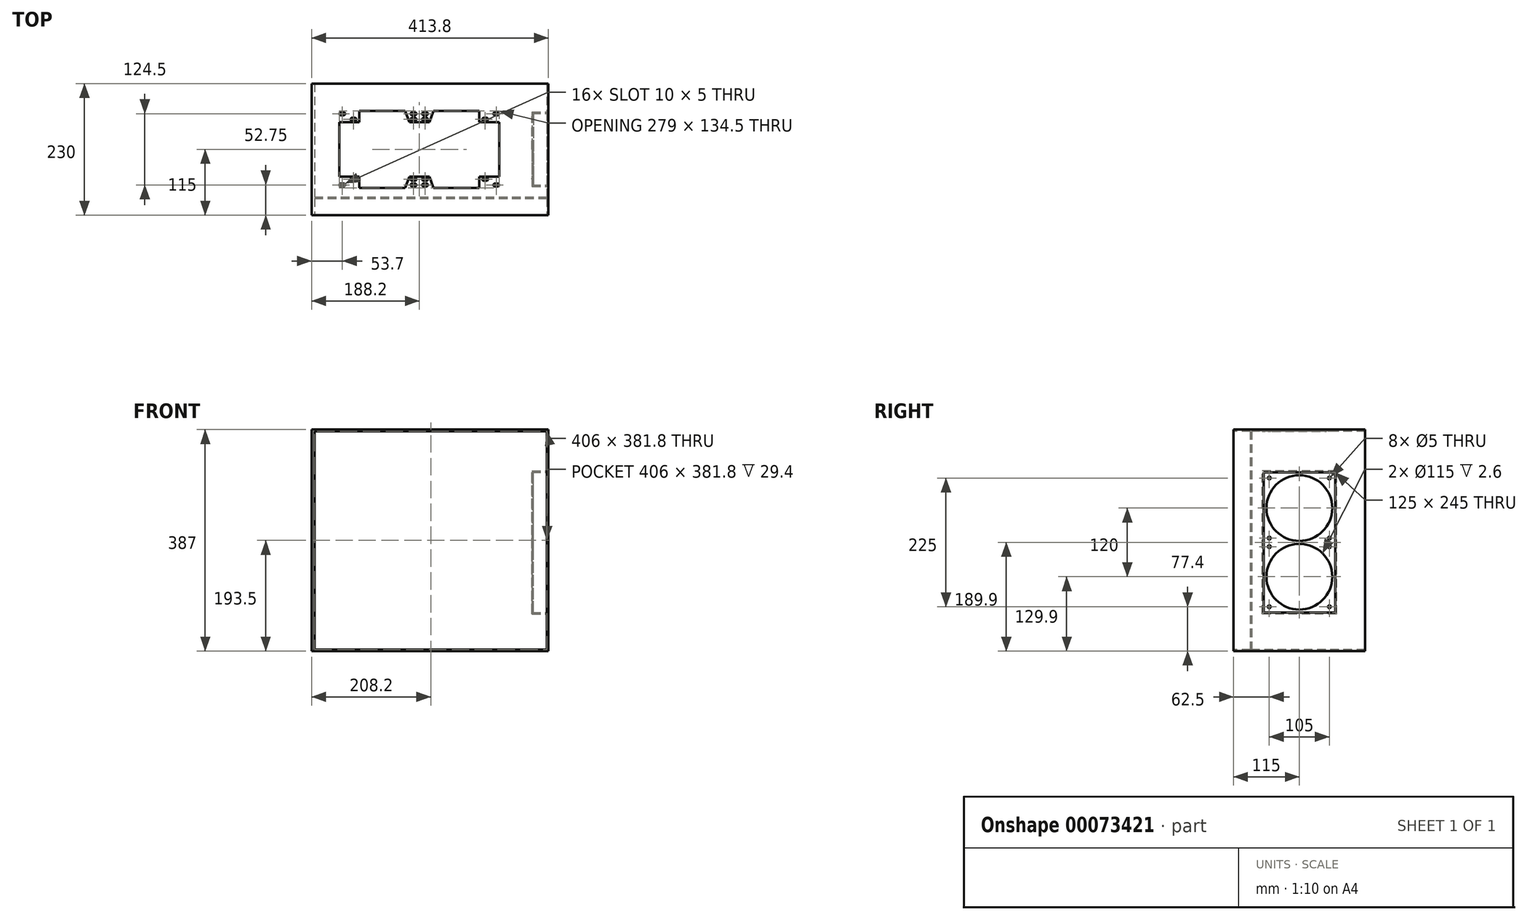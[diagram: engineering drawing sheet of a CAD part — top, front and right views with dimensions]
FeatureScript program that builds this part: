
annotation { "Feature Type Name" : "Feature", "Feature Type Description" : "" }
export const myFeature = defineFeature(function(context is Context, id is Id, definition is map)
    precondition{}
    {
        {
            var Q0;
            Q0=qCreatedBy(makeId("Front.planeOp"),FACE);
            var sketch = newSketch(context, id + "F0", { "sketchPlane" : qUnion([Q0])});
            skLineSegment(sketch, "E0.bottom", {"start": v(0, 0) * mm, "end": v(424, 0) * mm});
            skLineSegment(sketch, "E0.top", {"start": v(0, 397) * mm, "end": v(424, 397) * mm});
            skLineSegment(sketch, "E0.left", {"start": v(0, 0) * mm, "end": v(0, 397) * mm});
            skLineSegment(sketch, "E0.right", {"start": v(424, 0) * mm, "end": v(424, 397) * mm});
            skSolve(sketch);
        }
        {
            var Q0;
            Q0=makeQuery(id+"F0.imprint","IMPRINT",FACE,{"disambiguationData":[TD([[makeQuery(id+"F0.imprint","IMPRINT",EDGE,{"derivedFrom":sQuery(id+"F0.wireOp",EDGE,"E0.bottom")}),1.0]])]});
            extrude(context, id + "F1", {"entities" : qUnion([Q0]), "depth" : 230 * mm});
        }
        {
            var Q0;
            Q0=makeQuery(id+"F1.opExtrude","CAP_FACE",FACE,{"disambiguationData":[OSD([sQuery(id+"F0.wireOp",EDGE,"E0.bottom"),sQuery(id+"F0.wireOp",EDGE,"E0.top"),sQuery(id+"F0.wireOp",EDGE,"E0.left"),sQuery(id+"F0.wireOp",EDGE,"E0.right")])],"isStart":false});
            var sketch = newSketch(context, id + "F2", { "sketchPlane" : qUnion([Q0])});
            skLineSegment(sketch, "E1.bottom", {"start": v(5.2, 2.6) * mm, "end": v(411.2, 2.6) * mm});
            skLineSegment(sketch, "E1.top", {"start": v(5.2, 384.4) * mm, "end": v(411.2, 384.4) * mm});
            skLineSegment(sketch, "E1.left", {"start": v(5.2, 2.6) * mm, "end": v(5.2, 384.4) * mm});
            skLineSegment(sketch, "E1.right", {"start": v(411.2, 2.6) * mm, "end": v(411.2, 384.4) * mm});
            skSolve(sketch);
        }
        {
            var Q0;
            Q0 = qSketchRegion(id + "F2", true);
            extrude(context, id + "F3", {"entities" : qUnion([Q0]), "operationType" : NewBodyOperationType.REMOVE, "endBound" : BoundingType.THROUGH_ALL, "oppositeDirection" : true, "depth" : 198 * mm});
        }
        {
            var Q0;
            Q0=makeQuery(id+"F1.opExtrude","CAP_FACE",FACE,{"disambiguationData":[OSD([sQuery(id+"F0.wireOp",EDGE,"E0.bottom"),sQuery(id+"F0.wireOp",EDGE,"E0.top"),sQuery(id+"F0.wireOp",EDGE,"E0.left"),sQuery(id+"F0.wireOp",EDGE,"E0.right")])],"isStart":false});
            var sketch = newSketch(context, id + "F4", { "sketchPlane" : qUnion([Q0])});
            skLineSegment(sketch, "E2.bottom", {"start": v(0, 397) * mm, "end": v(424, 397) * mm});
            skLineSegment(sketch, "E2.top", {"start": v(0, 387) * mm, "end": v(413.8, 387) * mm});
            skLineSegment(sketch, "E2.left", {"start": v(0, 397) * mm, "end": v(0, 387) * mm});
            skLineSegment(sketch, "E3.bottom", {"start": v(424, 0) * mm, "end": v(413.8, 0) * mm});
            skLineSegment(sketch, "E3.left", {"start": v(424, 0) * mm, "end": v(424, 397) * mm});
            skLineSegment(sketch, "E3.right", {"start": v(413.8, 0) * mm, "end": v(413.8, 387) * mm});
            skSolve(sketch);
        }
        {
            var Q0;
            Q0 = qSketchRegion(id + "F4", true);
            extrude(context, id + "F5", {"entities" : qUnion([Q0]), "operationType" : NewBodyOperationType.REMOVE, "endBound" : BoundingType.THROUGH_ALL, "oppositeDirection" : true, "depth" : 25 * mm});
        }
        {
            var Q0;
            Q0=makeQuery(id+"F5.boolean.opBoolean","COPY",FACE,{"derivedFrom":makeQuery(id+"F5.opExtrude","SWEPT_FACE",FACE,{"disambiguationData":[OSD([sQuery(id+"F4.wireOp",EDGE,"E2.top")])]})});
            var sketch = newSketch(context, id + "F6", { "sketchPlane" : qUnion([Q0])});
            skLineSegment(sketch, "E4", {"start": v(413.8, -115) * mm, "end": v(0, -115) * mm, "construction": true});
            skPoint(sketch, "E5", {"position": v(303.2, -62.5) * mm});
            skPoint(sketch, "E6", {"position": v(303.2, -167.5) * mm});
            skPoint(sketch, "E7", {"position": v(322.7, -52.75) * mm});
            skPoint(sketch, "E8", {"position": v(322.7, -177.25) * mm});
            skPoint(sketch, "E9", {"position": v(198.2, -62.5) * mm});
            skPoint(sketch, "E10", {"position": v(198.2, -52.75) * mm});
            skPoint(sketch, "E11", {"position": v(198.2, -167.5) * mm});
            skPoint(sketch, "E12", {"position": v(198.2, -177.25) * mm});
            skPoint(sketch, "E13", {"position": v(178.2, -52.75) * mm});
            skPoint(sketch, "E14", {"position": v(178.2, -62.5) * mm});
            skPoint(sketch, "E15", {"position": v(178.2, -167.5) * mm});
            skPoint(sketch, "E16", {"position": v(178.2, -177.25) * mm});
            skPoint(sketch, "E17", {"position": v(73.2, -62.5) * mm});
            skPoint(sketch, "E18", {"position": v(73.2, -167.5) * mm});
            skPoint(sketch, "E19", {"position": v(53.7, -52.75) * mm});
            skPoint(sketch, "E20", {"position": v(53.7, -177.25) * mm});
            skLineSegment(sketch, "E21", {"start": v(48.7, -115) * mm, "end": v(48.7, -67.5) * mm});
            skLineSegment(sketch, "E22", {"start": v(48.7, -67.5) * mm, "end": v(83.2, -67.5) * mm});
            skLineSegment(sketch, "E23", {"start": v(83.2, -67.5) * mm, "end": v(83.2, -47.75) * mm});
            skLineSegment(sketch, "E24", {"start": v(83.2, -47.75) * mm, "end": v(163.2, -47.75) * mm});
            skLineSegment(sketch, "E25", {"start": v(163.2, -47.75) * mm, "end": v(170.7, -67.5) * mm});
            skLineSegment(sketch, "E26", {"start": v(170.7, -67.5) * mm, "end": v(205.7, -67.5) * mm});
            skLineSegment(sketch, "E27", {"start": v(205.7, -67.5) * mm, "end": v(213.2, -47.75) * mm});
            skLineSegment(sketch, "E28", {"start": v(213.2, -47.75) * mm, "end": v(293.2, -47.75) * mm});
            skLineSegment(sketch, "E29", {"start": v(293.2, -47.75) * mm, "end": v(293.2, -67.5) * mm});
            skLineSegment(sketch, "E30", {"start": v(293.2, -67.5) * mm, "end": v(327.7, -67.5) * mm});
            skLineSegment(sketch, "E31", {"start": v(327.7, -67.5) * mm, "end": v(327.7, -115) * mm});
            skLineSegment(sketch, "E32", {"start": v(178.2, -62.5) * mm, "end": v(198.2, -62.5) * mm, "construction": true});
            skPoint(sketch, "E33", {"position": v(188.2, -67.5) * mm});
            skPoint(sketch, "E34", {"position": v(188.2, -62.5) * mm});
            skLineSegment(sketch, "E35.MirrorCS", {"start": v(327.7, -162.5) * mm, "end": v(327.7, -115) * mm});
            skLineSegment(sketch, "E36.MirrorCS", {"start": v(293.2, -162.5) * mm, "end": v(327.7, -162.5) * mm});
            skLineSegment(sketch, "E37.MirrorCS", {"start": v(293.2, -182.25) * mm, "end": v(293.2, -162.5) * mm});
            skLineSegment(sketch, "E38.MirrorCS", {"start": v(213.2, -182.25) * mm, "end": v(293.2, -182.25) * mm});
            skLineSegment(sketch, "E39.MirrorCS", {"start": v(205.7, -162.5) * mm, "end": v(213.2, -182.25) * mm});
            skLineSegment(sketch, "E40.MirrorCS", {"start": v(170.7, -162.5) * mm, "end": v(205.7, -162.5) * mm});
            skLineSegment(sketch, "E41.MirrorCS", {"start": v(163.2, -182.25) * mm, "end": v(170.7, -162.5) * mm});
            skLineSegment(sketch, "E42.MirrorCS", {"start": v(83.2, -182.25) * mm, "end": v(163.2, -182.25) * mm});
            skLineSegment(sketch, "E43.MirrorCS", {"start": v(83.2, -162.5) * mm, "end": v(83.2, -182.25) * mm});
            skLineSegment(sketch, "E44.MirrorCS", {"start": v(48.7, -115) * mm, "end": v(48.7, -162.5) * mm});
            skLineSegment(sketch, "E45.MirrorCS", {"start": v(48.7, -162.5) * mm, "end": v(83.2, -162.5) * mm});
            skLineSegment(sketch, "E46.bottom", {"start": v(58.7, -50.25) * mm, "end": v(48.7, -50.25) * mm});
            skLineSegment(sketch, "E46.top", {"start": v(58.7, -55.25) * mm, "end": v(48.7, -55.25) * mm});
            skLineSegment(sketch, "E46.left", {"start": v(58.7, -50.25) * mm, "end": v(58.7, -55.25) * mm});
            skLineSegment(sketch, "E46.right", {"start": v(48.7, -50.25) * mm, "end": v(48.7, -55.25) * mm});
            skLineSegment(sketch, "E47.bottom", {"start": v(68.2, -60) * mm, "end": v(78.2, -60) * mm});
            skLineSegment(sketch, "E47.top", {"start": v(68.2, -65) * mm, "end": v(78.2, -65) * mm});
            skLineSegment(sketch, "E47.left", {"start": v(68.2, -60) * mm, "end": v(68.2, -65) * mm});
            skLineSegment(sketch, "E47.right", {"start": v(78.2, -60) * mm, "end": v(78.2, -65) * mm});
            skLineSegment(sketch, "E48.bottom", {"start": v(173.2, -50.25) * mm, "end": v(183.2, -50.25) * mm});
            skLineSegment(sketch, "E48.top", {"start": v(173.2, -55.25) * mm, "end": v(183.2, -55.25) * mm});
            skLineSegment(sketch, "E48.left", {"start": v(173.2, -50.25) * mm, "end": v(173.2, -55.25) * mm});
            skLineSegment(sketch, "E48.right", {"start": v(183.2, -50.25) * mm, "end": v(183.2, -55.25) * mm});
            skLineSegment(sketch, "E49.bottom", {"start": v(183.2, -60) * mm, "end": v(173.2, -60) * mm});
            skLineSegment(sketch, "E49.top", {"start": v(183.2, -65) * mm, "end": v(173.2, -65) * mm});
            skLineSegment(sketch, "E49.left", {"start": v(183.2, -60) * mm, "end": v(183.2, -65) * mm});
            skLineSegment(sketch, "E49.right", {"start": v(173.2, -60) * mm, "end": v(173.2, -65) * mm});
            skLineSegment(sketch, "E50.bottom", {"start": v(193.2, -50.25) * mm, "end": v(203.2, -50.25) * mm});
            skLineSegment(sketch, "E50.top", {"start": v(193.2, -55.25) * mm, "end": v(203.2, -55.25) * mm});
            skLineSegment(sketch, "E50.left", {"start": v(193.2, -50.25) * mm, "end": v(193.2, -55.25) * mm});
            skLineSegment(sketch, "E50.right", {"start": v(203.2, -50.25) * mm, "end": v(203.2, -55.25) * mm});
            skLineSegment(sketch, "E51.bottom", {"start": v(203.2, -60) * mm, "end": v(193.2, -60) * mm});
            skLineSegment(sketch, "E51.top", {"start": v(203.2, -65) * mm, "end": v(193.2, -65) * mm});
            skLineSegment(sketch, "E51.left", {"start": v(203.2, -60) * mm, "end": v(203.2, -65) * mm});
            skLineSegment(sketch, "E51.right", {"start": v(193.2, -60) * mm, "end": v(193.2, -65) * mm});
            skLineSegment(sketch, "E52.bottom", {"start": v(317.7, -50.25) * mm, "end": v(327.7, -50.25) * mm});
            skLineSegment(sketch, "E52.top", {"start": v(317.7, -55.25) * mm, "end": v(327.7, -55.25) * mm});
            skLineSegment(sketch, "E52.left", {"start": v(317.7, -50.25) * mm, "end": v(317.7, -55.25) * mm});
            skLineSegment(sketch, "E52.right", {"start": v(327.7, -50.25) * mm, "end": v(327.7, -55.25) * mm});
            skLineSegment(sketch, "E53.bottom", {"start": v(308.2, -60) * mm, "end": v(298.2, -60) * mm});
            skLineSegment(sketch, "E53.top", {"start": v(308.2, -65) * mm, "end": v(298.2, -65) * mm});
            skLineSegment(sketch, "E53.left", {"start": v(308.2, -60) * mm, "end": v(308.2, -65) * mm});
            skLineSegment(sketch, "E53.right", {"start": v(298.2, -60) * mm, "end": v(298.2, -65) * mm});
            skLineSegment(sketch, "E54.MirrorCS", {"start": v(48.7, -179.75) * mm, "end": v(48.7, -174.75) * mm});
            skLineSegment(sketch, "E55.MirrorCS", {"start": v(68.2, -165) * mm, "end": v(78.2, -165) * mm});
            skLineSegment(sketch, "E56.MirrorCS", {"start": v(68.2, -170) * mm, "end": v(78.2, -170) * mm});
            skLineSegment(sketch, "E57.MirrorCS", {"start": v(68.2, -170) * mm, "end": v(68.2, -165) * mm});
            skLineSegment(sketch, "E58.MirrorCS", {"start": v(58.7, -179.75) * mm, "end": v(48.7, -179.75) * mm});
            skLineSegment(sketch, "E59.MirrorCS", {"start": v(58.7, -179.75) * mm, "end": v(58.7, -174.75) * mm});
            skLineSegment(sketch, "E60.MirrorCS", {"start": v(78.2, -170) * mm, "end": v(78.2, -165) * mm});
            skLineSegment(sketch, "E61.MirrorCS", {"start": v(58.7, -174.75) * mm, "end": v(48.7, -174.75) * mm});
            skLineSegment(sketch, "E62.MirrorCS", {"start": v(193.2, -174.75) * mm, "end": v(203.2, -174.75) * mm});
            skLineSegment(sketch, "E63.MirrorCS", {"start": v(193.2, -179.75) * mm, "end": v(203.2, -179.75) * mm});
            skPoint(sketch, "E64.MirrorP", {"position": v(188.2, -167.5) * mm});
            skLineSegment(sketch, "E65.MirrorCS", {"start": v(173.2, -174.75) * mm, "end": v(183.2, -174.75) * mm});
            skLineSegment(sketch, "E66.MirrorCS", {"start": v(173.2, -170) * mm, "end": v(173.2, -165) * mm});
            skLineSegment(sketch, "E67.MirrorCS", {"start": v(203.2, -170) * mm, "end": v(203.2, -165) * mm});
            skPoint(sketch, "E68.MirrorP", {"position": v(188.2, -162.5) * mm});
            skLineSegment(sketch, "E69.MirrorCS", {"start": v(173.2, -179.75) * mm, "end": v(173.2, -174.75) * mm});
            skLineSegment(sketch, "E70.MirrorCS", {"start": v(193.2, -179.75) * mm, "end": v(193.2, -174.75) * mm});
            skLineSegment(sketch, "E71.MirrorCS", {"start": v(183.2, -165) * mm, "end": v(173.2, -165) * mm});
            skLineSegment(sketch, "E72.MirrorCS", {"start": v(178.2, -167.5) * mm, "end": v(198.2, -167.5) * mm, "construction": true});
            skLineSegment(sketch, "E73.MirrorCS", {"start": v(203.2, -165) * mm, "end": v(193.2, -165) * mm});
            skLineSegment(sketch, "E74.MirrorCS", {"start": v(203.2, -170) * mm, "end": v(193.2, -170) * mm});
            skLineSegment(sketch, "E75.MirrorCS", {"start": v(183.2, -170) * mm, "end": v(183.2, -165) * mm});
            skLineSegment(sketch, "E76.MirrorCS", {"start": v(193.2, -170) * mm, "end": v(193.2, -165) * mm});
            skLineSegment(sketch, "E77.MirrorCS", {"start": v(183.2, -179.75) * mm, "end": v(183.2, -174.75) * mm});
            skLineSegment(sketch, "E78.MirrorCS", {"start": v(173.2, -179.75) * mm, "end": v(183.2, -179.75) * mm});
            skLineSegment(sketch, "E79.MirrorCS", {"start": v(203.2, -179.75) * mm, "end": v(203.2, -174.75) * mm});
            skLineSegment(sketch, "E80.MirrorCS", {"start": v(183.2, -170) * mm, "end": v(173.2, -170) * mm});
            skLineSegment(sketch, "E81.MirrorCS", {"start": v(327.7, -179.75) * mm, "end": v(327.7, -174.75) * mm});
            skLineSegment(sketch, "E82.MirrorCS", {"start": v(308.2, -170) * mm, "end": v(298.2, -170) * mm});
            skLineSegment(sketch, "E83.MirrorCS", {"start": v(317.7, -179.75) * mm, "end": v(327.7, -179.75) * mm});
            skLineSegment(sketch, "E84.MirrorCS", {"start": v(298.2, -170) * mm, "end": v(298.2, -165) * mm});
            skLineSegment(sketch, "E85.MirrorCS", {"start": v(308.2, -165) * mm, "end": v(298.2, -165) * mm});
            skLineSegment(sketch, "E86.MirrorCS", {"start": v(308.2, -170) * mm, "end": v(308.2, -165) * mm});
            skLineSegment(sketch, "E87.MirrorCS", {"start": v(317.7, -174.75) * mm, "end": v(327.7, -174.75) * mm});
            skLineSegment(sketch, "E88.MirrorCS", {"start": v(317.7, -179.75) * mm, "end": v(317.7, -174.75) * mm});
            skSolve(sketch);
        }
        {
            var Q0;
            Q0 = qSketchRegion(id + "F6", true);
            extrude(context, id + "F7", {"entities" : qUnion([Q0]), "operationType" : NewBodyOperationType.REMOVE, "endBound" : BoundingType.UP_TO_NEXT, "oppositeDirection" : true, "depth" : 25 * mm});
        }
        {
            var Q0;
            Q0=makeQuery(id+"F5.boolean.opBoolean","COPY",FACE,{"derivedFrom":makeQuery(id+"F5.opExtrude","SWEPT_FACE",FACE,{"disambiguationData":[OSD([sQuery(id+"F4.wireOp",EDGE,"E3.right")])]})});
            var sketch = newSketch(context, id + "F8", { "sketchPlane" : qUnion([Q0])});
            skCircle(sketch, "E89", {"center": v(-167.5, 302.4) * mm, "radius": 2.5 * mm, "construction": true});
            skCircle(sketch, "E90", {"center": v(-62.5, 302.4) * mm, "radius": 2.5 * mm, "construction": true});
            skCircle(sketch, "E91", {"center": v(-167.5, 197.4) * mm, "radius": 2.5 * mm, "construction": true});
            skCircle(sketch, "E92", {"center": v(-62.5, 197.4) * mm, "radius": 2.5 * mm, "construction": true});
            skCircle(sketch, "E93", {"center": v(-167.5, 182.4) * mm, "radius": 2.5 * mm, "construction": true});
            skCircle(sketch, "E94", {"center": v(-62.5, 182.4) * mm, "radius": 2.5 * mm, "construction": true});
            skCircle(sketch, "E95", {"center": v(-167.5, 77.4) * mm, "radius": 2.5 * mm, "construction": true});
            skCircle(sketch, "E96", {"center": v(-62.5, 77.4) * mm, "radius": 2.5 * mm, "construction": true});
            skLineSegment(sketch, "E97", {"start": v(-115, 387) * mm, "end": v(-115, 0) * mm, "construction": true});
            skLineSegment(sketch, "E98.bottom", {"start": v(-177.5, 312.4) * mm, "end": v(-52.5, 312.4) * mm});
            skLineSegment(sketch, "E98.top", {"start": v(-177.5, 67.4) * mm, "end": v(-52.5, 67.4) * mm});
            skLineSegment(sketch, "E98.left", {"start": v(-177.5, 312.4) * mm, "end": v(-177.5, 67.4) * mm});
            skLineSegment(sketch, "E98.right", {"start": v(-52.5, 312.4) * mm, "end": v(-52.5, 67.4) * mm});
            skSolve(sketch);
        }
        {
            var Q0;
            Q0 = qSketchRegion(id + "F8", true);
            extrude(context, id + "F9", {"entities" : qUnion([Q0]), "operationType" : NewBodyOperationType.REMOVE, "endBound" : BoundingType.UP_TO_NEXT, "oppositeDirection" : true, "depth" : 46.66 * mm});
        }
        {
            var Q0;
            Q0=makeQuery(id+"F3.boolean.opBoolean","COPY",FACE,{"derivedFrom":makeQuery(id+"F3.opExtrude","SWEPT_FACE",FACE,{"disambiguationData":[OSD([sQuery(id+"F2.wireOp",EDGE,"E1.right")])]})});
            var sketch = newSketch(context, id + "F10", { "sketchPlane" : qUnion([Q0])});
            skLineSegment(sketch, "E99.bottom", {"start": v(177.5, 312.4) * mm, "end": v(52.5, 312.4) * mm});
            skLineSegment(sketch, "E99.top", {"start": v(177.5, 67.4) * mm, "end": v(52.5, 67.4) * mm});
            skLineSegment(sketch, "E99.left", {"start": v(177.5, 312.4) * mm, "end": v(177.5, 67.4) * mm});
            skLineSegment(sketch, "E99.right", {"start": v(52.5, 312.4) * mm, "end": v(52.5, 67.4) * mm});
            skLineSegment(sketch, "E100.bottom", {"start": v(49.9, 64.8) * mm, "end": v(180.1, 64.8) * mm});
            skLineSegment(sketch, "E100.top", {"start": v(49.9, 315) * mm, "end": v(180.1, 315) * mm});
            skLineSegment(sketch, "E100.left", {"start": v(49.9, 64.8) * mm, "end": v(49.9, 315) * mm});
            skLineSegment(sketch, "E100.right", {"start": v(180.1, 64.8) * mm, "end": v(180.1, 315) * mm});
            skSolve(sketch);
        }
        {
            var Q0;
            Q0 = qSketchRegion(id + "F10", true);
            extrude(context, id + "F11", {"entities" : qUnion([Q0]), "operationType" : NewBodyOperationType.ADD, "depth" : 26 * mm});
        }
        {
            var Q0;
            Q0=makeQuery(id+"F11.opExtrude","CAP_FACE",FACE,{"disambiguationData":[OSD([sQuery(id+"F10.wireOp",EDGE,"E99.bottom"),sQuery(id+"F10.wireOp",EDGE,"E99.top"),sQuery(id+"F10.wireOp",EDGE,"E99.left"),sQuery(id+"F10.wireOp",EDGE,"E99.right"),sQuery(id+"F10.wireOp",EDGE,"E100.bottom"),sQuery(id+"F10.wireOp",EDGE,"E100.top"),sQuery(id+"F10.wireOp",EDGE,"E100.left"),sQuery(id+"F10.wireOp",EDGE,"E100.right")])],"isStart":false});
            var sketch = newSketch(context, id + "F12", { "sketchPlane" : qUnion([Q0])});
            skLineSegment(sketch, "E101.bottom", {"start": v(177.5, 67.4) * mm, "end": v(52.5, 67.4) * mm});
            skLineSegment(sketch, "E101.top", {"start": v(177.5, 312.4) * mm, "end": v(52.5, 312.4) * mm});
            skLineSegment(sketch, "E101.left", {"start": v(177.5, 67.4) * mm, "end": v(177.5, 312.4) * mm});
            skLineSegment(sketch, "E101.right", {"start": v(52.5, 67.4) * mm, "end": v(52.5, 312.4) * mm});
            skSolve(sketch);
        }
        {
            var Q0;
            Q0 = qSketchRegion(id + "F12", true);
            extrude(context, id + "F13", {"entities" : qUnion([Q0]), "oppositeDirection" : true, "depth" : 2.6 * mm});
        }
        {
            var Q0;
            Q0=makeQuery(id+"F13.opExtrude","CAP_FACE",FACE,{"disambiguationData":[OSD([sQuery(id+"F12.wireOp",EDGE,"E101.bottom"),sQuery(id+"F12.wireOp",EDGE,"E101.top"),sQuery(id+"F12.wireOp",EDGE,"E101.left"),sQuery(id+"F12.wireOp",EDGE,"E101.right")])],"isStart":false});
            var sketch = newSketch(context, id + "F14", { "sketchPlane" : qUnion([Q0])});
            skCircle(sketch, "E102", {"center": v(-167.5, 302.4) * mm, "radius": 2.5 * mm});
            skCircle(sketch, "E103", {"center": v(-62.5, 302.4) * mm, "radius": 2.5 * mm});
            skCircle(sketch, "E104", {"center": v(-167.5, 197.4) * mm, "radius": 2.5 * mm});
            skCircle(sketch, "E105", {"center": v(-62.5, 197.4) * mm, "radius": 2.5 * mm});
            skCircle(sketch, "E106", {"center": v(-167.5, 182.4) * mm, "radius": 2.5 * mm});
            skCircle(sketch, "E107", {"center": v(-62.5, 182.4) * mm, "radius": 2.5 * mm});
            skCircle(sketch, "E108", {"center": v(-167.5, 77.4) * mm, "radius": 2.5 * mm});
            skCircle(sketch, "E109", {"center": v(-62.5, 77.4) * mm, "radius": 2.5 * mm});
            skLineSegment(sketch, "E110", {"start": v(-115, 312.4) * mm, "end": v(-115, 67.4) * mm, "construction": true});
            skLineSegment(sketch, "E111.bottom", {"start": v(-177.5, 312.4) * mm, "end": v(-52.5, 312.4) * mm, "construction": true});
            skLineSegment(sketch, "E111.top", {"start": v(-177.5, 67.4) * mm, "end": v(-52.5, 67.4) * mm, "construction": true});
            skLineSegment(sketch, "E111.left", {"start": v(-177.5, 312.4) * mm, "end": v(-177.5, 67.4) * mm, "construction": true});
            skLineSegment(sketch, "E111.right", {"start": v(-52.5, 312.4) * mm, "end": v(-52.5, 67.4) * mm, "construction": true});
            skCircle(sketch, "E112", {"center": v(-115, 249.9) * mm, "radius": 57.5 * mm});
            skCircle(sketch, "E113", {"center": v(-115, 129.9) * mm, "radius": 57.5 * mm});
            skSolve(sketch);
        }
        {
            var Q0;
            Q0 = qSketchRegion(id + "F14", true);
            extrude(context, id + "F15", {"entities" : qUnion([Q0]), "operationType" : NewBodyOperationType.REMOVE, "endBound" : BoundingType.UP_TO_NEXT, "oppositeDirection" : true, "depth" : 25 * mm});
        }
        {
            var Q0;
            Q0=makeQuery(id+"F7.boolean.opBoolean","COPY",EDGE,{"derivedFrom":makeQuery(id+"F7.opExtrude","SWEPT_EDGE",EDGE,{"disambiguationData":[OSD([sQuery(id+"F6.wireOp",EDGE,"E46.bottom"),sQuery(id+"F6.wireOp",EDGE,"E46.right")])]})});
            var Q1;
            Q1=makeQuery(id+"F7.boolean.opBoolean","COPY",EDGE,{"derivedFrom":makeQuery(id+"F7.opExtrude","SWEPT_EDGE",EDGE,{"disambiguationData":[OSD([sQuery(id+"F6.wireOp",EDGE,"E46.bottom"),sQuery(id+"F6.wireOp",EDGE,"E46.left")])]})});
            var Q2;
            Q2=makeQuery(id+"F7.boolean.opBoolean","COPY",EDGE,{"derivedFrom":makeQuery(id+"F7.opExtrude","SWEPT_EDGE",EDGE,{"disambiguationData":[OSD([sQuery(id+"F6.wireOp",EDGE,"E46.top"),sQuery(id+"F6.wireOp",EDGE,"E46.left")])]})});
            var Q3;
            Q3=makeQuery(id+"F7.boolean.opBoolean","COPY",EDGE,{"derivedFrom":makeQuery(id+"F7.opExtrude","SWEPT_EDGE",EDGE,{"disambiguationData":[OSD([sQuery(id+"F6.wireOp",EDGE,"E46.top"),sQuery(id+"F6.wireOp",EDGE,"E46.right")])]})});
            var Q4;
            Q4=makeQuery(id+"F7.boolean.opBoolean","COPY",EDGE,{"derivedFrom":makeQuery(id+"F7.opExtrude","SWEPT_EDGE",EDGE,{"disambiguationData":[OSD([sQuery(id+"F6.wireOp",EDGE,"E47.bottom"),sQuery(id+"F6.wireOp",EDGE,"E47.left")])]})});
            var Q5;
            Q5=makeQuery(id+"F7.boolean.opBoolean","COPY",EDGE,{"derivedFrom":makeQuery(id+"F7.opExtrude","SWEPT_EDGE",EDGE,{"disambiguationData":[OSD([sQuery(id+"F6.wireOp",EDGE,"E47.top"),sQuery(id+"F6.wireOp",EDGE,"E47.left")])]})});
            var Q6;
            Q6=makeQuery(id+"F7.boolean.opBoolean","COPY",EDGE,{"derivedFrom":makeQuery(id+"F7.opExtrude","SWEPT_EDGE",EDGE,{"disambiguationData":[OSD([sQuery(id+"F6.wireOp",EDGE,"E47.top"),sQuery(id+"F6.wireOp",EDGE,"E47.right")])]})});
            var Q7;
            Q7=makeQuery(id+"F7.boolean.opBoolean","COPY",EDGE,{"derivedFrom":makeQuery(id+"F7.opExtrude","SWEPT_EDGE",EDGE,{"disambiguationData":[OSD([sQuery(id+"F6.wireOp",EDGE,"E47.bottom"),sQuery(id+"F6.wireOp",EDGE,"E47.right")])]})});
            var Q8;
            Q8=makeQuery(id+"F7.boolean.opBoolean","COPY",EDGE,{"derivedFrom":makeQuery(id+"F7.opExtrude","SWEPT_EDGE",EDGE,{"disambiguationData":[OSD([sQuery(id+"F6.wireOp",EDGE,"E51.top"),sQuery(id+"F6.wireOp",EDGE,"E51.left")])]})});
            var Q9;
            Q9=makeQuery(id+"F7.boolean.opBoolean","COPY",EDGE,{"derivedFrom":makeQuery(id+"F7.opExtrude","SWEPT_EDGE",EDGE,{"disambiguationData":[OSD([sQuery(id+"F6.wireOp",EDGE,"E51.top"),sQuery(id+"F6.wireOp",EDGE,"E51.right")])]})});
            var Q10;
            Q10=makeQuery(id+"F7.boolean.opBoolean","COPY",EDGE,{"derivedFrom":makeQuery(id+"F7.opExtrude","SWEPT_EDGE",EDGE,{"disambiguationData":[OSD([sQuery(id+"F6.wireOp",EDGE,"E51.bottom"),sQuery(id+"F6.wireOp",EDGE,"E51.right")])]})});
            var Q11;
            Q11=makeQuery(id+"F7.boolean.opBoolean","COPY",EDGE,{"derivedFrom":makeQuery(id+"F7.opExtrude","SWEPT_EDGE",EDGE,{"disambiguationData":[OSD([sQuery(id+"F6.wireOp",EDGE,"E51.bottom"),sQuery(id+"F6.wireOp",EDGE,"E51.left")])]})});
            var Q12;
            Q12=makeQuery(id+"F7.boolean.opBoolean","COPY",EDGE,{"derivedFrom":makeQuery(id+"F7.opExtrude","SWEPT_EDGE",EDGE,{"disambiguationData":[OSD([sQuery(id+"F6.wireOp",EDGE,"E50.top"),sQuery(id+"F6.wireOp",EDGE,"E50.right")])]})});
            var Q13;
            Q13=makeQuery(id+"F7.boolean.opBoolean","COPY",EDGE,{"derivedFrom":makeQuery(id+"F7.opExtrude","SWEPT_EDGE",EDGE,{"disambiguationData":[OSD([sQuery(id+"F6.wireOp",EDGE,"E50.top"),sQuery(id+"F6.wireOp",EDGE,"E50.left")])]})});
            var Q14;
            Q14=makeQuery(id+"F7.boolean.opBoolean","COPY",EDGE,{"derivedFrom":makeQuery(id+"F7.opExtrude","SWEPT_EDGE",EDGE,{"disambiguationData":[OSD([sQuery(id+"F6.wireOp",EDGE,"E50.bottom"),sQuery(id+"F6.wireOp",EDGE,"E50.left")])]})});
            var Q15;
            Q15=makeQuery(id+"F7.boolean.opBoolean","COPY",EDGE,{"derivedFrom":makeQuery(id+"F7.opExtrude","SWEPT_EDGE",EDGE,{"disambiguationData":[OSD([sQuery(id+"F6.wireOp",EDGE,"E50.bottom"),sQuery(id+"F6.wireOp",EDGE,"E50.right")])]})});
            var Q16;
            Q16=makeQuery(id+"F7.boolean.opBoolean","COPY",EDGE,{"derivedFrom":makeQuery(id+"F7.opExtrude","SWEPT_EDGE",EDGE,{"disambiguationData":[OSD([sQuery(id+"F6.wireOp",EDGE,"E48.bottom"),sQuery(id+"F6.wireOp",EDGE,"E48.right")])]})});
            var Q17;
            Q17=makeQuery(id+"F7.boolean.opBoolean","COPY",EDGE,{"derivedFrom":makeQuery(id+"F7.opExtrude","SWEPT_EDGE",EDGE,{"disambiguationData":[OSD([sQuery(id+"F6.wireOp",EDGE,"E48.bottom"),sQuery(id+"F6.wireOp",EDGE,"E48.left")])]})});
            var Q18;
            Q18=makeQuery(id+"F7.boolean.opBoolean","COPY",EDGE,{"derivedFrom":makeQuery(id+"F7.opExtrude","SWEPT_EDGE",EDGE,{"disambiguationData":[OSD([sQuery(id+"F6.wireOp",EDGE,"E48.top"),sQuery(id+"F6.wireOp",EDGE,"E48.left")])]})});
            var Q19;
            Q19=makeQuery(id+"F7.boolean.opBoolean","COPY",EDGE,{"derivedFrom":makeQuery(id+"F7.opExtrude","SWEPT_EDGE",EDGE,{"disambiguationData":[OSD([sQuery(id+"F6.wireOp",EDGE,"E48.top"),sQuery(id+"F6.wireOp",EDGE,"E48.right")])]})});
            var Q20;
            Q20=makeQuery(id+"F7.boolean.opBoolean","COPY",EDGE,{"derivedFrom":makeQuery(id+"F7.opExtrude","SWEPT_EDGE",EDGE,{"disambiguationData":[OSD([sQuery(id+"F6.wireOp",EDGE,"E49.bottom"),sQuery(id+"F6.wireOp",EDGE,"E49.left")])]})});
            var Q21;
            Q21=makeQuery(id+"F7.boolean.opBoolean","COPY",EDGE,{"derivedFrom":makeQuery(id+"F7.opExtrude","SWEPT_EDGE",EDGE,{"disambiguationData":[OSD([sQuery(id+"F6.wireOp",EDGE,"E49.bottom"),sQuery(id+"F6.wireOp",EDGE,"E49.right")])]})});
            var Q22;
            Q22=makeQuery(id+"F7.boolean.opBoolean","COPY",EDGE,{"derivedFrom":makeQuery(id+"F7.opExtrude","SWEPT_EDGE",EDGE,{"disambiguationData":[OSD([sQuery(id+"F6.wireOp",EDGE,"E49.top"),sQuery(id+"F6.wireOp",EDGE,"E49.right")])]})});
            var Q23;
            Q23=makeQuery(id+"F7.boolean.opBoolean","COPY",EDGE,{"derivedFrom":makeQuery(id+"F7.opExtrude","SWEPT_EDGE",EDGE,{"disambiguationData":[OSD([sQuery(id+"F6.wireOp",EDGE,"E49.top"),sQuery(id+"F6.wireOp",EDGE,"E49.left")])]})});
            var Q24;
            Q24=makeQuery(id+"F7.boolean.opBoolean","COPY",EDGE,{"derivedFrom":makeQuery(id+"F7.opExtrude","SWEPT_EDGE",EDGE,{"disambiguationData":[OSD([sQuery(id+"F6.wireOp",EDGE,"E53.bottom"),sQuery(id+"F6.wireOp",EDGE,"E53.right")])]})});
            var Q25;
            Q25=makeQuery(id+"F7.boolean.opBoolean","COPY",EDGE,{"derivedFrom":makeQuery(id+"F7.opExtrude","SWEPT_EDGE",EDGE,{"disambiguationData":[OSD([sQuery(id+"F6.wireOp",EDGE,"E53.top"),sQuery(id+"F6.wireOp",EDGE,"E53.right")])]})});
            var Q26;
            Q26=makeQuery(id+"F7.boolean.opBoolean","COPY",EDGE,{"derivedFrom":makeQuery(id+"F7.opExtrude","SWEPT_EDGE",EDGE,{"disambiguationData":[OSD([sQuery(id+"F6.wireOp",EDGE,"E53.top"),sQuery(id+"F6.wireOp",EDGE,"E53.left")])]})});
            var Q27;
            Q27=makeQuery(id+"F7.boolean.opBoolean","COPY",EDGE,{"derivedFrom":makeQuery(id+"F7.opExtrude","SWEPT_EDGE",EDGE,{"disambiguationData":[OSD([sQuery(id+"F6.wireOp",EDGE,"E53.bottom"),sQuery(id+"F6.wireOp",EDGE,"E53.left")])]})});
            var Q28;
            Q28=makeQuery(id+"F7.boolean.opBoolean","COPY",EDGE,{"derivedFrom":makeQuery(id+"F7.opExtrude","SWEPT_EDGE",EDGE,{"disambiguationData":[OSD([sQuery(id+"F6.wireOp",EDGE,"E52.top"),sQuery(id+"F6.wireOp",EDGE,"E52.left")])]})});
            var Q29;
            Q29=makeQuery(id+"F7.boolean.opBoolean","COPY",EDGE,{"derivedFrom":makeQuery(id+"F7.opExtrude","SWEPT_EDGE",EDGE,{"disambiguationData":[OSD([sQuery(id+"F6.wireOp",EDGE,"E52.bottom"),sQuery(id+"F6.wireOp",EDGE,"E52.left")])]})});
            var Q30;
            Q30=makeQuery(id+"F7.boolean.opBoolean","COPY",EDGE,{"derivedFrom":makeQuery(id+"F7.opExtrude","SWEPT_EDGE",EDGE,{"disambiguationData":[OSD([sQuery(id+"F6.wireOp",EDGE,"E52.bottom"),sQuery(id+"F6.wireOp",EDGE,"E52.right")])]})});
            var Q31;
            Q31=makeQuery(id+"F7.boolean.opBoolean","COPY",EDGE,{"derivedFrom":makeQuery(id+"F7.opExtrude","SWEPT_EDGE",EDGE,{"disambiguationData":[OSD([sQuery(id+"F6.wireOp",EDGE,"E52.top"),sQuery(id+"F6.wireOp",EDGE,"E52.right")])]})});
            var Q32;
            Q32=makeQuery(id+"F7.boolean.opBoolean","COPY",EDGE,{"derivedFrom":makeQuery(id+"F7.opExtrude","SWEPT_EDGE",EDGE,{"disambiguationData":[OSD([sQuery(id+"F6.wireOp",EDGE,"E81.MirrorCS"),sQuery(id+"F6.wireOp",EDGE,"E87.MirrorCS")])]})});
            var Q33;
            Q33=makeQuery(id+"F7.boolean.opBoolean","COPY",EDGE,{"derivedFrom":makeQuery(id+"F7.opExtrude","SWEPT_EDGE",EDGE,{"disambiguationData":[OSD([sQuery(id+"F6.wireOp",EDGE,"E81.MirrorCS"),sQuery(id+"F6.wireOp",EDGE,"E83.MirrorCS")])]})});
            var Q34;
            Q34=makeQuery(id+"F7.boolean.opBoolean","COPY",EDGE,{"derivedFrom":makeQuery(id+"F7.opExtrude","SWEPT_EDGE",EDGE,{"disambiguationData":[OSD([sQuery(id+"F6.wireOp",EDGE,"E83.MirrorCS"),sQuery(id+"F6.wireOp",EDGE,"E88.MirrorCS")])]})});
            var Q35;
            Q35=makeQuery(id+"F7.boolean.opBoolean","COPY",EDGE,{"derivedFrom":makeQuery(id+"F7.opExtrude","SWEPT_EDGE",EDGE,{"disambiguationData":[OSD([sQuery(id+"F6.wireOp",EDGE,"E87.MirrorCS"),sQuery(id+"F6.wireOp",EDGE,"E88.MirrorCS")])]})});
            var Q36;
            Q36=makeQuery(id+"F7.boolean.opBoolean","COPY",EDGE,{"derivedFrom":makeQuery(id+"F7.opExtrude","SWEPT_EDGE",EDGE,{"disambiguationData":[OSD([sQuery(id+"F6.wireOp",EDGE,"E82.MirrorCS"),sQuery(id+"F6.wireOp",EDGE,"E86.MirrorCS")])]})});
            var Q37;
            Q37=makeQuery(id+"F7.boolean.opBoolean","COPY",EDGE,{"derivedFrom":makeQuery(id+"F7.opExtrude","SWEPT_EDGE",EDGE,{"disambiguationData":[OSD([sQuery(id+"F6.wireOp",EDGE,"E85.MirrorCS"),sQuery(id+"F6.wireOp",EDGE,"E86.MirrorCS")])]})});
            var Q38;
            Q38=makeQuery(id+"F7.boolean.opBoolean","COPY",EDGE,{"derivedFrom":makeQuery(id+"F7.opExtrude","SWEPT_EDGE",EDGE,{"disambiguationData":[OSD([sQuery(id+"F6.wireOp",EDGE,"E84.MirrorCS"),sQuery(id+"F6.wireOp",EDGE,"E85.MirrorCS")])]})});
            var Q39;
            Q39=makeQuery(id+"F7.boolean.opBoolean","COPY",EDGE,{"derivedFrom":makeQuery(id+"F7.opExtrude","SWEPT_EDGE",EDGE,{"disambiguationData":[OSD([sQuery(id+"F6.wireOp",EDGE,"E82.MirrorCS"),sQuery(id+"F6.wireOp",EDGE,"E84.MirrorCS")])]})});
            var Q40;
            Q40=makeQuery(id+"F7.boolean.opBoolean","COPY",EDGE,{"derivedFrom":makeQuery(id+"F7.opExtrude","SWEPT_EDGE",EDGE,{"disambiguationData":[OSD([sQuery(id+"F6.wireOp",EDGE,"E67.MirrorCS"),sQuery(id+"F6.wireOp",EDGE,"E73.MirrorCS")])]})});
            var Q41;
            Q41=makeQuery(id+"F7.boolean.opBoolean","COPY",EDGE,{"derivedFrom":makeQuery(id+"F7.opExtrude","SWEPT_EDGE",EDGE,{"disambiguationData":[OSD([sQuery(id+"F6.wireOp",EDGE,"E73.MirrorCS"),sQuery(id+"F6.wireOp",EDGE,"E76.MirrorCS")])]})});
            var Q42;
            Q42=makeQuery(id+"F7.boolean.opBoolean","COPY",EDGE,{"derivedFrom":makeQuery(id+"F7.opExtrude","SWEPT_EDGE",EDGE,{"disambiguationData":[OSD([sQuery(id+"F6.wireOp",EDGE,"E74.MirrorCS"),sQuery(id+"F6.wireOp",EDGE,"E76.MirrorCS")])]})});
            var Q43;
            Q43=makeQuery(id+"F7.boolean.opBoolean","COPY",EDGE,{"derivedFrom":makeQuery(id+"F7.opExtrude","SWEPT_EDGE",EDGE,{"disambiguationData":[OSD([sQuery(id+"F6.wireOp",EDGE,"E67.MirrorCS"),sQuery(id+"F6.wireOp",EDGE,"E74.MirrorCS")])]})});
            var Q44;
            Q44=makeQuery(id+"F7.boolean.opBoolean","COPY",EDGE,{"derivedFrom":makeQuery(id+"F7.opExtrude","SWEPT_EDGE",EDGE,{"disambiguationData":[OSD([sQuery(id+"F6.wireOp",EDGE,"E62.MirrorCS"),sQuery(id+"F6.wireOp",EDGE,"E79.MirrorCS")])]})});
            var Q45;
            Q45=makeQuery(id+"F7.boolean.opBoolean","COPY",EDGE,{"derivedFrom":makeQuery(id+"F7.opExtrude","SWEPT_EDGE",EDGE,{"disambiguationData":[OSD([sQuery(id+"F6.wireOp",EDGE,"E62.MirrorCS"),sQuery(id+"F6.wireOp",EDGE,"E70.MirrorCS")])]})});
            var Q46;
            Q46=makeQuery(id+"F7.boolean.opBoolean","COPY",EDGE,{"derivedFrom":makeQuery(id+"F7.opExtrude","SWEPT_EDGE",EDGE,{"disambiguationData":[OSD([sQuery(id+"F6.wireOp",EDGE,"E63.MirrorCS"),sQuery(id+"F6.wireOp",EDGE,"E70.MirrorCS")])]})});
            var Q47;
            Q47=makeQuery(id+"F7.boolean.opBoolean","COPY",EDGE,{"derivedFrom":makeQuery(id+"F7.opExtrude","SWEPT_EDGE",EDGE,{"disambiguationData":[OSD([sQuery(id+"F6.wireOp",EDGE,"E63.MirrorCS"),sQuery(id+"F6.wireOp",EDGE,"E79.MirrorCS")])]})});
            var Q48;
            Q48=makeQuery(id+"F7.boolean.opBoolean","COPY",EDGE,{"derivedFrom":makeQuery(id+"F7.opExtrude","SWEPT_EDGE",EDGE,{"disambiguationData":[OSD([sQuery(id+"F6.wireOp",EDGE,"E77.MirrorCS"),sQuery(id+"F6.wireOp",EDGE,"E78.MirrorCS")])]})});
            var Q49;
            Q49=makeQuery(id+"F7.boolean.opBoolean","COPY",EDGE,{"derivedFrom":makeQuery(id+"F7.opExtrude","SWEPT_EDGE",EDGE,{"disambiguationData":[OSD([sQuery(id+"F6.wireOp",EDGE,"E65.MirrorCS"),sQuery(id+"F6.wireOp",EDGE,"E77.MirrorCS")])]})});
            var Q50;
            Q50=makeQuery(id+"F7.boolean.opBoolean","COPY",EDGE,{"derivedFrom":makeQuery(id+"F7.opExtrude","SWEPT_EDGE",EDGE,{"disambiguationData":[OSD([sQuery(id+"F6.wireOp",EDGE,"E65.MirrorCS"),sQuery(id+"F6.wireOp",EDGE,"E69.MirrorCS")])]})});
            var Q51;
            Q51=makeQuery(id+"F7.boolean.opBoolean","COPY",EDGE,{"derivedFrom":makeQuery(id+"F7.opExtrude","SWEPT_EDGE",EDGE,{"disambiguationData":[OSD([sQuery(id+"F6.wireOp",EDGE,"E69.MirrorCS"),sQuery(id+"F6.wireOp",EDGE,"E78.MirrorCS")])]})});
            var Q52;
            Q52=makeQuery(id+"F7.boolean.opBoolean","COPY",EDGE,{"derivedFrom":makeQuery(id+"F7.opExtrude","SWEPT_EDGE",EDGE,{"disambiguationData":[OSD([sQuery(id+"F6.wireOp",EDGE,"E66.MirrorCS"),sQuery(id+"F6.wireOp",EDGE,"E71.MirrorCS")])]})});
            var Q53;
            Q53=makeQuery(id+"F7.boolean.opBoolean","COPY",EDGE,{"derivedFrom":makeQuery(id+"F7.opExtrude","SWEPT_EDGE",EDGE,{"disambiguationData":[OSD([sQuery(id+"F6.wireOp",EDGE,"E66.MirrorCS"),sQuery(id+"F6.wireOp",EDGE,"E80.MirrorCS")])]})});
            var Q54;
            Q54=makeQuery(id+"F7.boolean.opBoolean","COPY",EDGE,{"derivedFrom":makeQuery(id+"F7.opExtrude","SWEPT_EDGE",EDGE,{"disambiguationData":[OSD([sQuery(id+"F6.wireOp",EDGE,"E75.MirrorCS"),sQuery(id+"F6.wireOp",EDGE,"E80.MirrorCS")])]})});
            var Q55;
            Q55=makeQuery(id+"F7.boolean.opBoolean","COPY",EDGE,{"derivedFrom":makeQuery(id+"F7.opExtrude","SWEPT_EDGE",EDGE,{"disambiguationData":[OSD([sQuery(id+"F6.wireOp",EDGE,"E71.MirrorCS"),sQuery(id+"F6.wireOp",EDGE,"E75.MirrorCS")])]})});
            var Q56;
            Q56=makeQuery(id+"F7.boolean.opBoolean","COPY",EDGE,{"derivedFrom":makeQuery(id+"F7.opExtrude","SWEPT_EDGE",EDGE,{"disambiguationData":[OSD([sQuery(id+"F6.wireOp",EDGE,"E55.MirrorCS"),sQuery(id+"F6.wireOp",EDGE,"E60.MirrorCS")])]})});
            var Q57;
            Q57=makeQuery(id+"F7.boolean.opBoolean","COPY",EDGE,{"derivedFrom":makeQuery(id+"F7.opExtrude","SWEPT_EDGE",EDGE,{"disambiguationData":[OSD([sQuery(id+"F6.wireOp",EDGE,"E56.MirrorCS"),sQuery(id+"F6.wireOp",EDGE,"E60.MirrorCS")])]})});
            var Q58;
            Q58=makeQuery(id+"F7.boolean.opBoolean","COPY",EDGE,{"derivedFrom":makeQuery(id+"F7.opExtrude","SWEPT_EDGE",EDGE,{"disambiguationData":[OSD([sQuery(id+"F6.wireOp",EDGE,"E56.MirrorCS"),sQuery(id+"F6.wireOp",EDGE,"E57.MirrorCS")])]})});
            var Q59;
            Q59=makeQuery(id+"F7.boolean.opBoolean","COPY",EDGE,{"derivedFrom":makeQuery(id+"F7.opExtrude","SWEPT_EDGE",EDGE,{"disambiguationData":[OSD([sQuery(id+"F6.wireOp",EDGE,"E55.MirrorCS"),sQuery(id+"F6.wireOp",EDGE,"E57.MirrorCS")])]})});
            var Q60;
            Q60=makeQuery(id+"F7.boolean.opBoolean","COPY",EDGE,{"derivedFrom":makeQuery(id+"F7.opExtrude","SWEPT_EDGE",EDGE,{"disambiguationData":[OSD([sQuery(id+"F6.wireOp",EDGE,"E54.MirrorCS"),sQuery(id+"F6.wireOp",EDGE,"E61.MirrorCS")])]})});
            var Q61;
            Q61=makeQuery(id+"F7.boolean.opBoolean","COPY",EDGE,{"derivedFrom":makeQuery(id+"F7.opExtrude","SWEPT_EDGE",EDGE,{"disambiguationData":[OSD([sQuery(id+"F6.wireOp",EDGE,"E54.MirrorCS"),sQuery(id+"F6.wireOp",EDGE,"E58.MirrorCS")])]})});
            var Q62;
            Q62=makeQuery(id+"F7.boolean.opBoolean","COPY",EDGE,{"derivedFrom":makeQuery(id+"F7.opExtrude","SWEPT_EDGE",EDGE,{"disambiguationData":[OSD([sQuery(id+"F6.wireOp",EDGE,"E58.MirrorCS"),sQuery(id+"F6.wireOp",EDGE,"E59.MirrorCS")])]})});
            var Q63;
            Q63=makeQuery(id+"F7.boolean.opBoolean","COPY",EDGE,{"derivedFrom":makeQuery(id+"F7.opExtrude","SWEPT_EDGE",EDGE,{"disambiguationData":[OSD([sQuery(id+"F6.wireOp",EDGE,"E59.MirrorCS"),sQuery(id+"F6.wireOp",EDGE,"E61.MirrorCS")])]})});
            fillet(context, id + "F16", {"entities" : qUnion([Q0, Q1, Q2, Q3, Q4, Q5, Q6, Q7, Q8, Q9, Q10, Q11, Q12, Q13, Q14, Q15, Q16, Q17, Q18, Q19, Q20, Q21, Q22, Q23, Q24, Q25, Q26, Q27, Q28, Q29, Q30, Q31, Q32, Q33, Q34, Q35, Q36, Q37, Q38, Q39, Q40, Q41, Q42, Q43, Q44, Q45, Q46, Q47, Q48, Q49, Q50, Q51, Q52, Q53, Q54, Q55, Q56, Q57, Q58, Q59, Q60, Q61, Q62, Q63]), "radius" : 2.5 * mm, "tangentPropagation" : true, "allowEdgeOverflow" : false});
        }
        {
            var Q0;
            Q0=makeQuery(id+"F1.opExtrude","CAP_FACE",FACE,{"disambiguationData":[OSD([sQuery(id+"F0.wireOp",EDGE,"E0.bottom"),sQuery(id+"F0.wireOp",EDGE,"E0.top"),sQuery(id+"F0.wireOp",EDGE,"E0.left"),sQuery(id+"F0.wireOp",EDGE,"E0.right")])],"isStart":false});
            cPlane(context, id + "F17", {"entities" : qUnion([Q0]), "cplaneType" : CPlaneType.OFFSET, "offset" : 198 * mm, "oppositeDirection" : true, "width" : 150 * mm, "height" : 150 * mm});
        }
        {
            var Q0;
            Q0=qCreatedBy(id+"F17.planeOp",FACE);
            var sketch = newSketch(context, id + "F18", { "sketchPlane" : qUnion([Q0])});
            skLineSegment(sketch, "E114.bottom", {"start": v(5.2, 384.4) * mm, "end": v(411.2, 384.4) * mm});
            skLineSegment(sketch, "E114.top", {"start": v(5.2, 2.6) * mm, "end": v(411.2, 2.6) * mm});
            skLineSegment(sketch, "E114.left", {"start": v(5.2, 384.4) * mm, "end": v(5.2, 2.6) * mm});
            skLineSegment(sketch, "E114.right", {"start": v(411.2, 384.4) * mm, "end": v(411.2, 2.6) * mm});
            skSolve(sketch);
        }
        {
            var Q0;
            Q0=makeQuery(id+"F1.opExtrude","CAP_FACE",FACE,{"disambiguationData":[OSD([sQuery(id+"F0.wireOp",EDGE,"E0.bottom"),sQuery(id+"F0.wireOp",EDGE,"E0.top"),sQuery(id+"F0.wireOp",EDGE,"E0.left"),sQuery(id+"F0.wireOp",EDGE,"E0.right")])],"isStart":false});
            cPlane(context, id + "F19", {"entities" : qUnion([Q0]), "cplaneType" : CPlaneType.OFFSET, "offset" : (230 - 198) * mm, "oppositeDirection" : true, "width" : 150 * mm, "height" : 150 * mm});
        }
        {
            var Q0;
            Q0=qCreatedBy(id+"F19.planeOp",FACE);
            var sketch = newSketch(context, id + "F20", { "sketchPlane" : qUnion([Q0])});
            skLineSegment(sketch, "E115.bottom", {"start": v(5.2, 384.4) * mm, "end": v(411.2, 384.4) * mm});
            skLineSegment(sketch, "E115.top", {"start": v(5.2, 2.6) * mm, "end": v(411.2, 2.6) * mm});
            skLineSegment(sketch, "E115.left", {"start": v(5.2, 384.4) * mm, "end": v(5.2, 2.6) * mm});
            skLineSegment(sketch, "E115.right", {"start": v(411.2, 384.4) * mm, "end": v(411.2, 2.6) * mm});
            skSolve(sketch);
        }
        {
            var Q0;
            Q0 = qSketchRegion(id + "F20", true);
            extrude(context, id + "F21", {"entities" : qUnion([Q0]), "operationType" : NewBodyOperationType.ADD, "depth" : 2.6 * mm});
        }
    });
